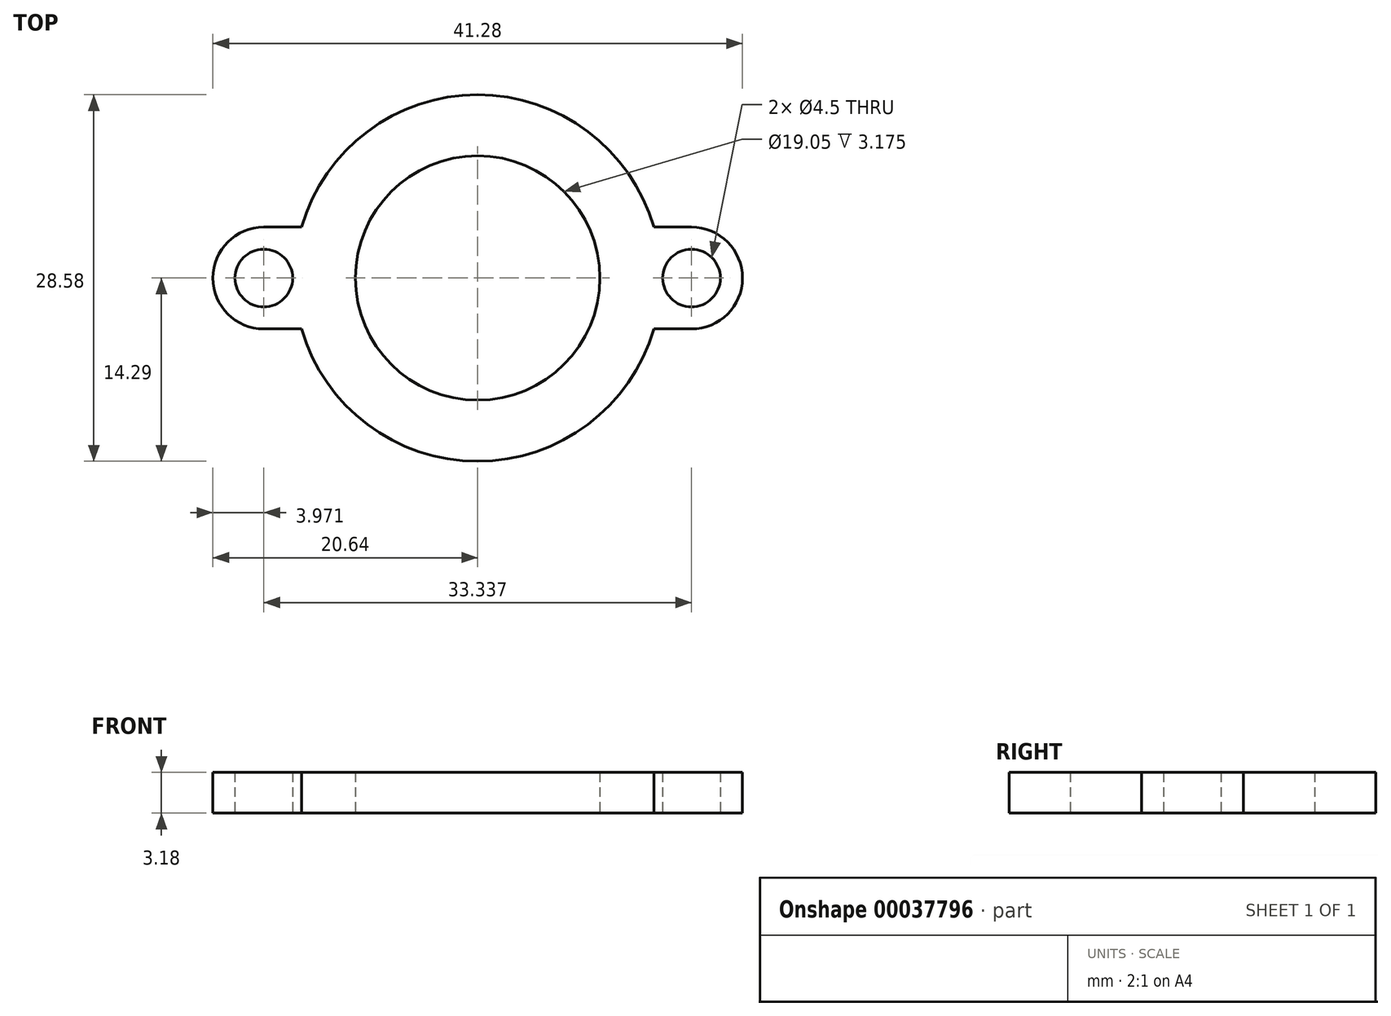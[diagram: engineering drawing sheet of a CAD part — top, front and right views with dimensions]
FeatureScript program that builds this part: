
annotation { "Feature Type Name" : "Feature", "Feature Type Description" : "" }
export const myFeature = defineFeature(function(context is Context, id is Id, definition is map)
    precondition{}
    {
        {
            var Q0;
            Q0=qCreatedBy(makeId("Top.planeOp"),FACE);
            var sketch = newSketch(context, id + "F0", { "sketchPlane" : qUnion([Q0])});
            skCircle(sketch, "E0", {"center": v(0, 0) * mm, "radius": 9.53 * mm});
            skLineSegment(sketch, "E1", {"start": v(-16.67, 0) * mm, "end": v(16.67, 0) * mm, "construction": true});
            skArc(sketch, "E2", {"start": v(13.73, 3.97) * mm, "mid": v(0, 14.29) * mm, "end": v(-13.73, 3.97) * mm});
            skArc(sketch, "E3", {"start": v(-13.73, -3.97) * mm, "mid": v(0, -14.29) * mm, "end": v(13.73, -3.97) * mm});
            skArc(sketch, "E4", {"start": v(-16.67, 3.97) * mm, "mid": v(-20.64, 0) * mm, "end": v(-16.67, -3.97) * mm});
            skArc(sketch, "E5", {"start": v(16.67, -3.97) * mm, "mid": v(20.64, 0) * mm, "end": v(16.67, 3.97) * mm});
            skLineSegment(sketch, "E6", {"start": v(-16.67, 3.97) * mm, "end": v(-16.67, -3.97) * mm, "construction": true});
            skLineSegment(sketch, "E7", {"start": v(16.67, 3.97) * mm, "end": v(16.67, -3.97) * mm, "construction": true});
            skLineSegment(sketch, "E8", {"start": v(16.67, -3.97) * mm, "end": v(13.73, -3.97) * mm});
            skLineSegment(sketch, "E9", {"start": v(16.67, 3.97) * mm, "end": v(13.73, 3.97) * mm});
            skLineSegment(sketch, "E10", {"start": v(-16.67, -3.97) * mm, "end": v(-13.73, -3.97) * mm});
            skLineSegment(sketch, "E11", {"start": v(-16.67, 3.97) * mm, "end": v(-13.73, 3.97) * mm});
            skCircle(sketch, "E12", {"center": v(-16.67, 0) * mm, "radius": 2.25 * mm});
            skCircle(sketch, "E13", {"center": v(16.67, 0) * mm, "radius": 2.25 * mm});
            skSolve(sketch);
        }
        {
            var Q0;
            Q0 = qSketchRegion(id + "F0", true);
            extrude(context, id + "F1", {"entities" : qUnion([Q0]), "depth" : 3.17 * mm});
        }
    });
